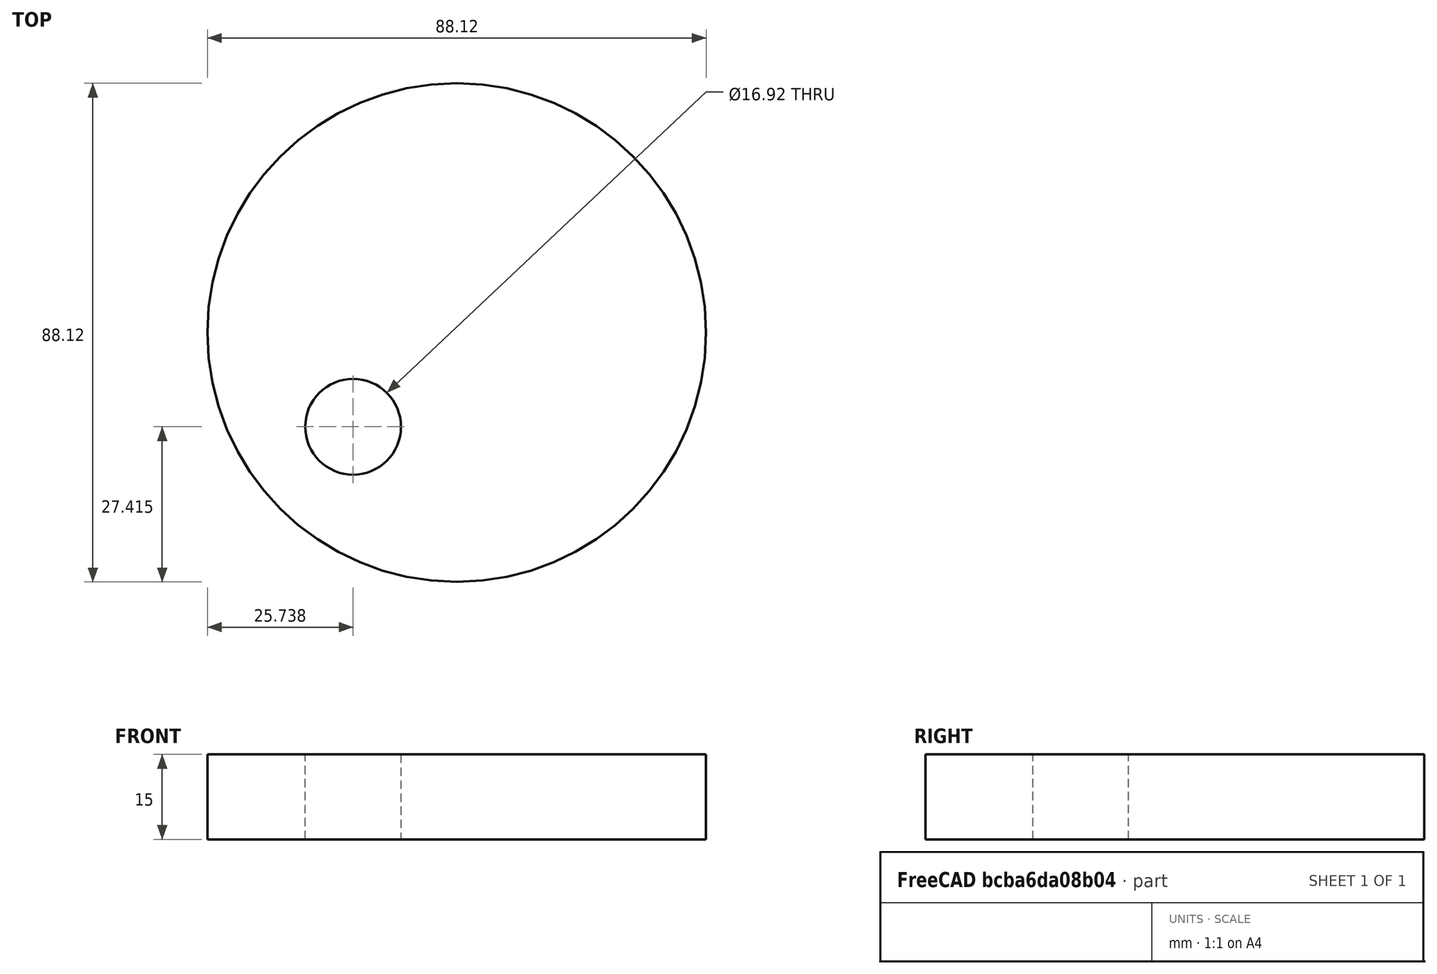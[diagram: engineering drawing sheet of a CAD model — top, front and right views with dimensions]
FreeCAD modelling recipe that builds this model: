
FCSTD DOCUMENT  (FreeCAD 1.0R39319 (Git))
Label: first_part_of_robot
License: All rights reserved
LicenseURL: https://en.wikipedia.org/wiki/All_rights_reserved
objects: Sketcher::SketchObject×2, PartDesign::Pad×1, PartDesign::Pocket×1, PartDesign::Body×1
note: 11 computed .brp shape members not serialized (recipe doc carries the construction recipe); baked Part::Feature solids carry a one-line shape summary decoded from their .brp

FEATURE [Sketcher::SketchObject] Sketch
  ArcFitTolerance = 1e-06
  AttachmentSupport = -> [XY_Plane]
  FullyConstrained = false
  MakeInternals = false
  MapMode = 5
  sketch-geometry (1):
    g0: Circle CenterX=-26.7012 CenterY=-18.0473 CenterZ=0 NormalX=0 NormalY=0 NormalZ=1 AngleXU=0 Radius=44.0583
FEATURE [PartDesign::Pad] Pad
  Direction = (0,0,1)
  Length = 15
  Length2 = 10
  Profile = -> Sketch [Edge1]
  ReferenceAxis = -> Sketch [N_Axis]
  Refine = true
  Suppressed = false
  Type = 0
FEATURE [Sketcher::SketchObject] Sketch001
  ArcFitTolerance = 1e-06
  AttachmentSupport = -> [Pad]
  FullyConstrained = false
  MakeInternals = false
  MapMode = 5
  Placement = pos=(0,0,15) rot=(0,0,1;0rad)
  sketch-geometry (1):
    g0: Circle CenterX=-45.0223 CenterY=-34.6954 CenterZ=0 NormalX=0 NormalY=0 NormalZ=1 AngleXU=0 Radius=8.4578
FEATURE [PartDesign::Pocket] Pocket
  BaseFeature = -> Pad
  Direction = (0,0,-1)
  Length = 15
  Length2 = 5
  Profile = -> Sketch001
  ReferenceAxis = -> Sketch001 [N_Axis]
  Refine = true
  Suppressed = false
  Type = 0
FEATURE [PartDesign::Body] Body  label="Тело"
  AllowCompound = false
  Group = -> [Sketch,Pad,Sketch001,Pocket]
  Origin = -> Origin
  Tip = -> Pocket
